# Revit family: BOX BV PLUS
name_source: partatom
category: Modelos genéricos
revit_build: Autodesk Revit 2017 (Build: 20160225_1515(x64)
units: mm (PartAtom-declared; Revit-internal decimal feet)

## family parameters
Compartido = No
Corte con vacíos al cargar = No
Cota de conector redondo = Diámetro de uso
Puede alojar armadura = No
Punto de cálculo de habitación = No
Se basa en plano de trabajo = No
Siempre vertical = Sí
Tipo de pieza = Normal

## types (6) — shared parameters
Fabricante = Casals Ventilación
L = 41 mm  [stored 0.134514 ft]
URL = www.casals.com
e = 30 mm

## per-type parameters (varying)
| type | A | B | C | D | E | I | J |
| BOX BV PLUS 7/7 | 500 mm  [stored 1.64042 ft] | 500 mm  [stored 1.64042 ft] | 770 mm  [stored 2.52625 ft] | 208 mm | 102 mm | 135 mm  [stored 0.442913 ft] | 440 mm  [stored 1.44357 ft] |
| BOX BV PLUS 9/9 | 550 mm | 550 mm | 820 mm  [stored 2.69029 ft] | 260 mm  [stored 0.853018 ft] | 82 mm  [stored 0.269029 ft] | 122 mm | 490 mm  [stored 1.60761 ft] |
| BOX BV PLUS 10/10 | 600 mm | 600 mm | 870 mm  [stored 2.85433 ft] | 291 mm  [stored 0.954724 ft] | 80 mm  [stored 0.262467 ft] | 136 mm | 540 mm  [stored 1.77165 ft] |
| BOX BV PLUS 12/12 | 700 mm  [stored 2.29659 ft] | 700 mm  [stored 2.29659 ft] | 970 mm  [stored 3.18241 ft] | 344 mm | 103 mm | 152 mm  [stored 0.498688 ft] | 640 mm  [stored 2.09974 ft] |
| BOX BV PLUS 15/15 | 800 mm  [stored 2.62467 ft] | 800 mm  [stored 2.62467 ft] | 1070 mm  [stored 3.5105 ft] | 404 mm  [stored 1.32546 ft] | 113 mm  [stored 0.370735 ft] | 164 mm | 740 mm  [stored 2.42782 ft] |
| BOX BV PLUS 18/18 | 950 mm  [stored 3.1168 ft] | 950 mm  [stored 3.1168 ft] | 1220 mm  [stored 4.00262 ft] | 483 mm | 139 mm  [stored 0.456037 ft] | 197 mm | 890 mm  [stored 2.91995 ft] |

note: column(s) folded — value = type name in every type: Modelo

note: [stored X ft] marks values corroborated as IEEE doubles in the binary element streams (Revit-internal decimal feet)
